# Revit family: IS_Ceraplan_BD338_BIM_FR
name_source: partatom
category: Plumbing Fixtures
units: mm (PartAtom-declared; Revit-internal decimal feet)

## family parameters
Always vertical = No
Cut with Voids When Loaded = No
OmniClass Number = 23.45.55.17
OmniClass Title = Mixing Faucets
Part Type = Normal
Room Calculation Point = No
Round Connector Dimension = Use Diameter
Shared = No
Work Plane-Based = No

## types (1)
- BD338AA - Ceraplan Single lever kitchen mixer Rim-Montedwith high tubular spout with pull-down spray 2 functions Blue Start low pressure - Chrome
    Accessories = https://www.idealstandard.fr
    AreaUnits = millimetres
    Auteur = Ideal Standard
    BIMObjectName = IS_IdealStandard_Sinktaps_Ceraplan_BD338
    BIMobject category = Taps & Mixers
    BIMobject category code = sanitary-taps-mixers
    BIMobject main category = Sanitary
    BIMobject main category code = sanitary
    BarCode = 3800861104988
    Bim-NomDuProjet = IS_IdealStandard_Sinktaps_Ceraplan_BD338
    Brand = Ideal Standard
    Brand url = http://www.idealstandard.fr
    Caractéristiques = Mitigeur de cuisine sur bride avec bec tube haut avec douchette extractible 2 fonctions Blue Start basse pression
    Category = Taps & Mixer
    CodeBarre = 3800861104988
    Color = Chrome
    ConnectionType = Plomberie
    ConseilsDInstallation = https://www.idealstandard.fr
    Couleur = Chrome
    CoûtDeRemplacement = 0
    CurrencyUnit = €
    CurrentRevision = 1
    Date of publishing = 25/03/2022
    DateDeCréation = 25/03/2022
    Description = Ceraplan Mitigeur de cuisine sur bride avec bec tube haut avec douchette extractible 2 fonctions Blue Start basse pression
    DescriptionDeLaRobinetterie = Ceraplan Mitigeur de cuisine sur bride avec bec tube haut avec douchette extractible 2 fonctions Blue Start basse pression
    Dimensions = 118 x 256 x 394 mm
    DurationUnit = Years
    DuréeDeGarantieDesPièces = 5
    DuréeGarantie = 5
    DétailGarantie = https://www.idealstandard.fr
    Edition number = 1
    EffectuéPar = 25/03/2022
    FaucetFunction = Kitchen Mixer
    FaucetOperation = Single Lever Kitchen mixer
    FaucetTopDescription = Single Lever Kitchen mixer
    FaucetType = Kitchen Mixer
    Features = Mitigeur de cuisine sur bride avec bec tube haut avec douchette rétractable 2 fonctions Blue Start basse pression
    Finish = Chrome
    Finition = Chrome
    Forme = cylindrique
    GTIN code = https://3800861104988
    Hauteur = 394 mm
    Help = https://www.idealstandard.fr
    IFC Classification = Sanitary Terminal
    IfcExportAs = IfcValveType
    IfcExportType = FAUCET
    InformationsProduit = https://www.idealstandard.fr
    Installation instructions = https://www.idealstandard.fr
    InstallationInstructions = https://www.idealstandard.fr
    Largeur = 118 mm
    LinearUnits = millimeters
    Longueur = 256 mm
    MainColor = Chrome
    MaintenanceInformation = https://www.idealstandard.fr
    Manufacturer = Ideal Standard
    Manufacturer name = Ideal Standard
    ManufacturerURL = https://www.idealstandard.fr
    Marque = Ideal Standard
    Material = Brass
    Material main = Brass
    Matériel = Laiton
    Model = BD338AA
    ModelNumber = BD338AA
    ModelReference = Ceraplan Single lever kitchen mixer Rim-Montedwith high tubular spout with pull-down spray 2 functions Blue Start low pressure
    Mécanisme = levier unique
    NBS Reference Code = 45-35-70/345
    NBS Reference Description = Water supply fittings for sinks
    Name = Sinktaps_Ceraplan_BD338_IdealStandard
    NettWeight = 3,5 Kg
    Nom = Sinktaps_Ceraplan_BD338_IdealStandard
    NominalDepth = 256 mm
    NominalHeight = 394 mm
    NominalLength = 256 mm
    NominalWidth = 118 mm
    OmniClass Code = 23-31 11 00
    OmniClass Description = Faucets
    PiècesDétachées = https://www.idealstandard.fr
    PoidsNet = 3,5 Kg
    PoignéesDePréhension = No
    PressionDeFonctionnement = 0
    Product Guid = e7369b5b-144a-4618-a898-7e0cdc2562c7
    Product SKU = BD338
    Product certification = https://www.idealstandard.fr
    Product data url = https://bimobject.com
    Product family = CERAPLAN
    Product group = Kitchen Mixers
    Product name = Ceraplan Single lever kitchen mixer Rim-Montedwith high tubular spout with pull-down spray 2 functions Blue Start low pressure
    Product url = https://www.idealstandard.fr
    ProductInformation = https://www.idealstandard.fr
    Profondeur = 256 mm
    QR code = http://bimobject.com
    Raccordement = https://www.idealstandard.fr
    Révision = 1
    Shape = cylindrical
    Size = 118 x 256 x 394 mm
    Space = Internal
    SpareParts = https://www.idealstandard.fr
    Technical description = https://www.idealstandard.fr
    TechnologieDeLaRobinetterie = Mitigeur de cuisine à levier unique
    TestDePression = 10
    TypeDeRobinetterie = robinet de cuisine
    UNSPSC Code = 301815
    URL = https://www.idealstandard.fr
    Uniclass 1.4 Code = L725111
    Uniclass 1.4 Description = Mixer taps
    Uniclass 2.0 Code = PR-35-79-79
    Uniclass 2.0 Description = Sink Water Supply Fittings
    Uniclass 2015 Code = Pr_40_20_87_84
    Uniclass 2015 Name = Sink taps
    Uniclass2015Code = Pr_40_20_87_84
    Uniclass2015Title = Sink taps
    Uniclass2015Version = v1.25
    Uniformat II Code = PR-35-79-79
    Uniformat II Description = SinkWaterSupplyFittings
    UnitéDeMesure = millimètres
    UnitéDeTemps = années
    UnitéMonétaire = euro
    UrlDuFabricant = https://www.idealstandard.fr
    UsageDeLaRobinetterie = robinet de cuisine
    Version = 1
    VolumeUnits = Litres
    WRASURL = https://www.wrasapprovals.co.uk
    WarrantyDescription = manufacturer warranty
    WarrantyDurationParts = 5
    WarrantyDurationUnit = Years
    WorkingPressure = Low Pressure
    Youtube clip = https://www.youtube.com

## geometry (parser evidence)
native form markers: Sweep x3
no freeform markers — native parametric forms only
